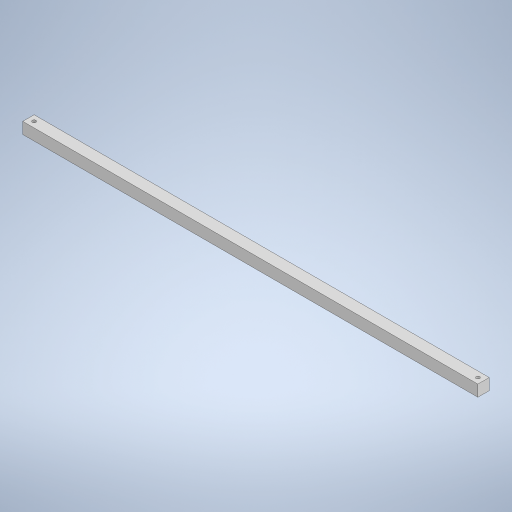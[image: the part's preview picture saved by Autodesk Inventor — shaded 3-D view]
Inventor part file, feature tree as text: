
AUTODESK INVENTOR PART (.ipt)
format: ipt  version: 2023 (Build 270158000, 158)  size: 243,200 bytes
history: native  units: mm
features: sketch x2, other x1, extrude x1, hole x1
ambient origin geometry x8: Origin, YZ Plane, XZ Plane, XY Plane, X Axis, Y Axis, Z Axis, Center Point
bodies: Body1 (feature_tree)
feature tree (5):
  other  "ソリッド1"
  extrude  "押し出し1"  Depth=400.0mm
  hole  "穴1"  [1 undecoded]
  sketch  "スケッチ1"
  sketch  "スケッチ4"
note: 1 required parameter value undecoded (feature->parameter linkage not recoverable at this tier; creation-order binding heuristic only, values carry confidence <= 0.55)
